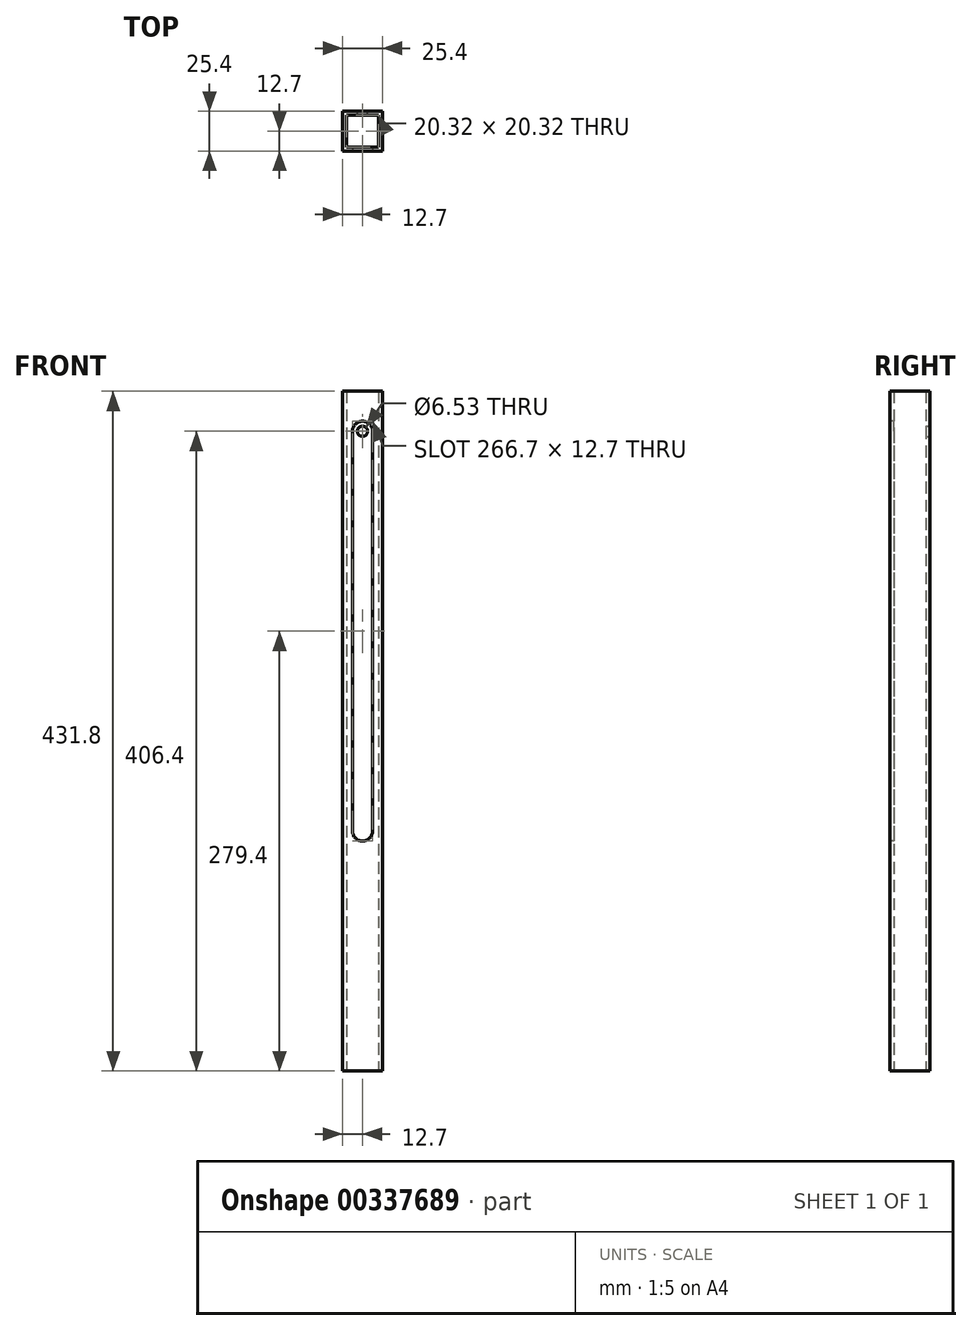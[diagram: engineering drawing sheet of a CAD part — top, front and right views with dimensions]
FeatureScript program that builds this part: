
annotation { "Feature Type Name" : "Feature", "Feature Type Description" : "" }
export const myFeature = defineFeature(function(context is Context, id is Id, definition is map)
    precondition{}
    {
        {
            var Q0;
            Q0=qCreatedBy(makeId("Front.planeOp"),FACE);
            var sketch = newSketch(context, id + "F0", { "sketchPlane" : qUnion([Q0])});
            skLineSegment(sketch, "E0.bottom", {"start": v(0, 0) * mm, "end": v(25.4, 0) * mm});
            skLineSegment(sketch, "E0.top", {"start": v(0, -431.8) * mm, "end": v(25.4, -431.8) * mm});
            skLineSegment(sketch, "E0.left", {"start": v(0, 0) * mm, "end": v(0, -431.8) * mm});
            skLineSegment(sketch, "E0.right", {"start": v(25.4, 0) * mm, "end": v(25.4, -431.8) * mm});
            skLineSegment(sketch, "E1.left", {"start": v(0, 0) * mm, "end": v(0, -25.4) * mm, "construction": true});
            skSolve(sketch);
        }
        {
            var Q0;
            Q0=makeQuery(id+"F0.imprint","IMPRINT",FACE,{"disambiguationData":[TD([[makeQuery(id+"F0.imprint","IMPRINT",EDGE,{"derivedFrom":sQuery(id+"F0.wireOp",EDGE,"E0.bottom")}),-1.0]])]});
            extrude(context, id + "F1", {"entities" : qUnion([Q0]), "depth" : 25.4 * mm});
        }
        {
            var Q0;
            Q0=makeQuery(id+"F1.opExtrude","SWEPT_FACE",FACE,{"disambiguationData":[OSD([sQuery(id+"F0.wireOp",EDGE,"E0.bottom")])]});
            var Q1;
            Q1=makeQuery(id+"F1.opExtrude","SWEPT_FACE",FACE,{"disambiguationData":[OSD([sQuery(id+"F0.wireOp",EDGE,"E0.top")])]});
            shell(context, id + "F2", {"entities" : qUnion([Q0, Q1]), "thickness" : 2.54 * mm});
        }
        {
            var Q0;
            Q0=makeQuery(id+"F1.opExtrude","CAP_FACE",FACE,{"disambiguationData":[OSD([sQuery(id+"F0.wireOp",EDGE,"E0.bottom"),sQuery(id+"F0.wireOp",EDGE,"E0.top"),sQuery(id+"F0.wireOp",EDGE,"E0.left"),sQuery(id+"F0.wireOp",EDGE,"E0.right")])],"isStart":false});
            var sketch = newSketch(context, id + "F3", { "sketchPlane" : qUnion([Q0])});
            skLineSegment(sketch, "E2.bottom", {"start": v(0, 0) * mm, "end": v(12.7, 0) * mm, "construction": true});
            skLineSegment(sketch, "E2.left", {"start": v(0, 0) * mm, "end": v(0, -25.4) * mm, "construction": true});
            skLineSegment(sketch, "E2.right", {"start": v(12.7, 0) * mm, "end": v(12.7, -19.05) * mm, "construction": true});
            skLineSegment(sketch, "E3.top", {"start": v(0, 0) * mm, "end": v(6.35, 0) * mm, "construction": true});
            skLineSegment(sketch, "E3.left", {"start": v(0, -9.08) * mm, "end": v(0, 0) * mm, "construction": true});
            skArc(sketch, "E4", {"start": v(19.05, -25.4) * mm, "mid": v(12.7, -19.05) * mm, "end": v(6.35, -25.4) * mm});
            skArc(sketch, "E5", {"start": v(6.35, -279.4) * mm, "mid": v(12.7, -285.75) * mm, "end": v(19.05, -279.4) * mm});
            skLineSegment(sketch, "E6", {"start": v(6.35, -25.4) * mm, "end": v(6.35, -279.4) * mm});
            skLineSegment(sketch, "E7", {"start": v(19.05, -25.4) * mm, "end": v(19.05, -279.4) * mm});
            skSolve(sketch);
        }
        {
            var Q0;
            Q0=makeQuery(id+"F3.imprint","IMPRINT",FACE,{"disambiguationData":[TD([[makeQuery(id+"F3.imprint","IMPRINT",EDGE,{"derivedFrom":sQuery(id+"F3.wireOp",EDGE,"E4")}),1.0]])]});
            extrude(context, id + "F4", {"entities" : qUnion([Q0]), "operationType" : NewBodyOperationType.REMOVE, "oppositeDirection" : true, "depth" : 6.35 * mm});
        }
        {
            var Q0;
            Q0=makeQuery(id+"F1.opExtrude","CAP_FACE",FACE,{"disambiguationData":[OSD([sQuery(id+"F0.wireOp",EDGE,"E0.bottom"),sQuery(id+"F0.wireOp",EDGE,"E0.top"),sQuery(id+"F0.wireOp",EDGE,"E0.left"),sQuery(id+"F0.wireOp",EDGE,"E0.right")])],"isStart":true});
            var sketch = newSketch(context, id + "F5", { "sketchPlane" : qUnion([Q0])});
            skLineSegment(sketch, "E8.bottom", {"start": v(0, 0) * mm, "end": v(-12.7, 0) * mm, "construction": true});
            skLineSegment(sketch, "E8.top", {"start": v(0, -25.4) * mm, "end": v(-12.7, -25.4) * mm, "construction": true});
            skLineSegment(sketch, "E8.left", {"start": v(0, 0) * mm, "end": v(0, -25.4) * mm, "construction": true});
            skLineSegment(sketch, "E8.right", {"start": v(-12.7, 0) * mm, "end": v(-12.7, -25.4) * mm, "construction": true});
            skCircle(sketch, "E9", {"center": v(-12.7, -25.4) * mm, "radius": 3.26 * mm});
            skSolve(sketch);
        }
        {
            var Q0;
            Q0=makeQuery(id+"F5.imprint","IMPRINT",FACE,{"disambiguationData":[TD([[makeQuery(id+"F5.imprint","IMPRINT",EDGE,{"derivedFrom":sQuery(id+"F5.wireOp",EDGE,"E9")}),1.0]])]});
            extrude(context, id + "F6", {"entities" : qUnion([Q0]), "operationType" : NewBodyOperationType.REMOVE, "oppositeDirection" : true, "depth" : 2.54 * mm});
        }
    });
